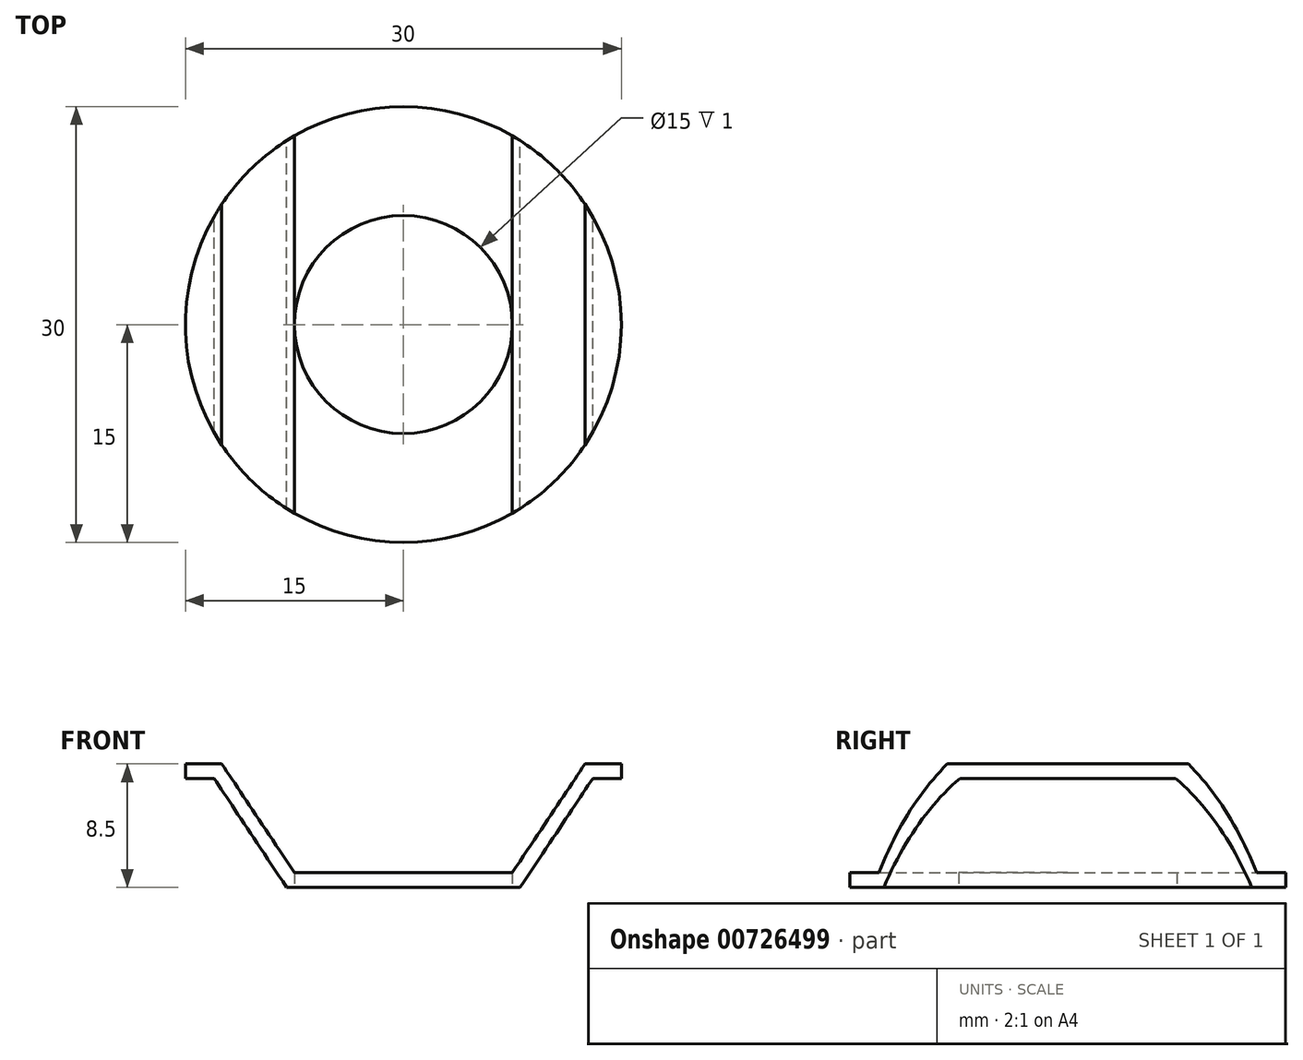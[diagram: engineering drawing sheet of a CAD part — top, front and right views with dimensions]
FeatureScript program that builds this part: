
annotation { "Feature Type Name" : "Feature", "Feature Type Description" : "" }
export const myFeature = defineFeature(function(context is Context, id is Id, definition is map)
    precondition{}
    {
        {
            var Q0;
            Q0=qCreatedBy(makeId("Front.planeOp"),FACE);
            var sketch = newSketch(context, id + "F0", { "sketchPlane" : qUnion([Q0])});
            skLineSegment(sketch, "E0", {"start": v(0, 0) * mm, "end": v(-7.5, 0) * mm});
            skLineSegment(sketch, "E1", {"start": v(-7.5, 0) * mm, "end": v(-12.5, 7.5) * mm});
            skLineSegment(sketch, "E2", {"start": v(-12.5, 7.5) * mm, "end": v(-15, 7.5) * mm});
            skLineSegment(sketch, "E3.0", {"start": v(-13.04, 6.5) * mm, "end": v(-15, 6.5) * mm});
            skLineSegment(sketch, "E3.1", {"start": v(-8.04, -1) * mm, "end": v(-13.04, 6.5) * mm});
            skLineSegment(sketch, "E3.2", {"start": v(0, -1) * mm, "end": v(-8.04, -1) * mm});
            skLineSegment(sketch, "E4", {"start": v(-15, 6.5) * mm, "end": v(-15, 7.5) * mm});
            skLineSegment(sketch, "E5", {"start": v(0, -1) * mm, "end": v(0, 0) * mm});
            skLineSegment(sketch, "E6.MirrorCS", {"start": v(0, 0) * mm, "end": v(7.5, 0) * mm});
            skLineSegment(sketch, "E7.MirrorCS", {"start": v(0, -1) * mm, "end": v(8.04, -1) * mm});
            skLineSegment(sketch, "E8.MirrorCS", {"start": v(7.5, 0) * mm, "end": v(12.5, 7.5) * mm});
            skLineSegment(sketch, "E9.MirrorCS", {"start": v(8.04, -1) * mm, "end": v(13.04, 6.5) * mm});
            skLineSegment(sketch, "E10.MirrorCS", {"start": v(12.5, 7.5) * mm, "end": v(15, 7.5) * mm});
            skLineSegment(sketch, "E11.MirrorCS", {"start": v(13.04, 6.5) * mm, "end": v(15, 6.5) * mm});
            skLineSegment(sketch, "E12.MirrorCS", {"start": v(15, 6.5) * mm, "end": v(15, 7.5) * mm});
            skSolve(sketch);
        }
        {
            var Q0;
            Q0 = qSketchRegion(id + "F0", true);
            extrude(context, id + "F1", {"entities" : qUnion([Q0]), "depth" : 30 * mm, "offsetDistance" : 25 * mm});
        }
        {
            var Q0;
            Q0=qCreatedBy(makeId("Top.planeOp"),FACE);
            var sketch = newSketch(context, id + "F2", { "sketchPlane" : qUnion([Q0])});
            skCircle(sketch, "E13", {"center": v(0, -15) * mm, "radius": 15 * mm});
            skCircle(sketch, "E14.0", {"center": v(0, -15) * mm, "radius": 7.5 * mm});
            skSolve(sketch);
        }
        {
            var Q0;
            Q0 = qSketchRegion(id + "F2", true);
            extrude(context, id + "F3", {"entities" : qUnion([Q0]), "operationType" : NewBodyOperationType.INTERSECT, "endBound" : BoundingType.THROUGH_ALL, "depth" : 25 * mm, "offsetDistance" : 25 * mm, "hasSecondDirection" : true, "secondDirectionOppositeDirection" : true, "secondDirectionDepth" : 25 * mm});
        }
    });
